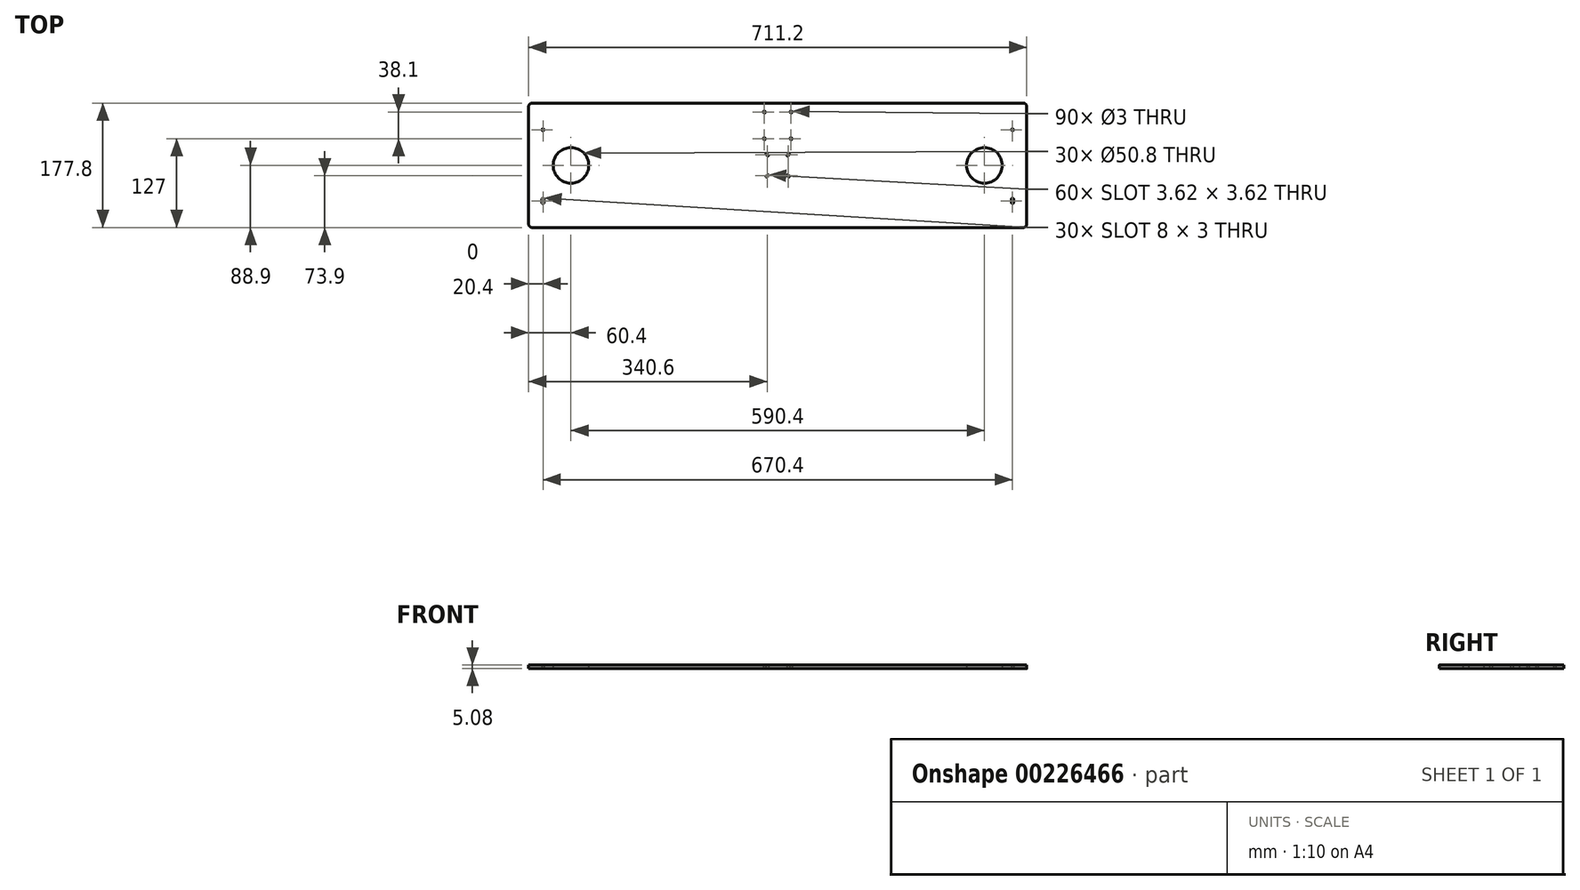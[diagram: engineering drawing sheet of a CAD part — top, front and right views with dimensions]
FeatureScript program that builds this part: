
annotation { "Feature Type Name" : "Feature", "Feature Type Description" : "" }
export const myFeature = defineFeature(function(context is Context, id is Id, definition is map)
    precondition{}
    {
        {
            var Q0;
            Q0=qCreatedBy(makeId("Top.planeOp"),FACE);
            var sketch = newSketch(context, id + "F0", { "sketchPlane" : qUnion([Q0])});
            skLineSegment(sketch, "E0.bottom", {"start": v(350.6, 88.9) * mm, "end": v(-350.6, 88.9) * mm});
            skLineSegment(sketch, "E0.top", {"start": v(350.6, -88.9) * mm, "end": v(-350.6, -88.9) * mm});
            skLineSegment(sketch, "E0.left", {"start": v(355.6, 83.9) * mm, "end": v(355.6, -83.9) * mm});
            skLineSegment(sketch, "E0.right", {"start": v(-355.6, 83.9) * mm, "end": v(-355.6, -83.9) * mm});
            skPoint(sketch, "E0.middle", {"position": v(0, 0) * mm});
            skCircle(sketch, "E1", {"center": v(-335.2, 50.8) * mm, "radius": 1.5 * mm});
            skArc(sketch, "E2", {"start": v(-336.7, -53.3) * mm, "mid": v(-335.2, -54.8) * mm, "end": v(-333.7, -53.3) * mm});
            skArc(sketch, "E3", {"start": v(-333.7, -48.3) * mm, "mid": v(-335.2, -46.8) * mm, "end": v(-336.7, -48.3) * mm});
            skLineSegment(sketch, "E4", {"start": v(-333.7, -48.3) * mm, "end": v(-333.7, -53.3) * mm});
            skLineSegment(sketch, "E5", {"start": v(-336.7, -48.3) * mm, "end": v(-336.7, -53.3) * mm});
            skPoint(sketch, "E6", {"position": v(-333.7, -50.8) * mm});
            skLineSegment(sketch, "E7", {"start": v(-335.2, 50.8) * mm, "end": v(-335.2, -50.8) * mm, "construction": true});
            skPoint(sketch, "E8", {"position": v(-335.2, 0) * mm});
            skLineSegment(sketch, "E9", {"start": v(0, 88.9) * mm, "end": v(0, -88.9) * mm, "construction": true});
            skLineSegment(sketch, "E10.MirrorCS", {"start": v(333.7, -48.3) * mm, "end": v(333.7, -53.3) * mm});
            skLineSegment(sketch, "E11.MirrorCS", {"start": v(336.7, -48.3) * mm, "end": v(336.7, -53.3) * mm});
            skArc(sketch, "E12.MirrorCS", {"start": v(336.7, -53.3) * mm, "mid": v(335.2, -54.8) * mm, "end": v(333.7, -53.3) * mm});
            skCircle(sketch, "E13.MirrorC", {"center": v(335.2, 50.8) * mm, "radius": 1.5 * mm});
            skArc(sketch, "E14.MirrorCS", {"start": v(333.7, -48.3) * mm, "mid": v(335.2, -46.8) * mm, "end": v(336.7, -48.3) * mm});
            skPoint(sketch, "E15.MirrorP", {"position": v(333.7, -50.8) * mm});
            skPoint(sketch, "E16.MirrorP", {"position": v(335.2, 0) * mm});
            skLineSegment(sketch, "E17.MirrorCS", {"start": v(335.2, 50.8) * mm, "end": v(335.2, -50.8) * mm, "construction": true});
            skPoint(sketch, "E18.visualSharp", {"position": v(355.6, 88.9) * mm});
            skArc(sketch, "E18.filletArc", {"start": v(355.6, 83.9) * mm, "mid": v(354.14, 87.44) * mm, "end": v(350.6, 88.9) * mm});
            skPoint(sketch, "E19.visualSharp", {"position": v(355.6, -88.9) * mm});
            skArc(sketch, "E19.filletArc", {"start": v(350.6, -88.9) * mm, "mid": v(354.14, -87.44) * mm, "end": v(355.6, -83.9) * mm});
            skPoint(sketch, "E20.visualSharp", {"position": v(-355.6, -88.9) * mm});
            skArc(sketch, "E20.filletArc", {"start": v(-355.6, -83.9) * mm, "mid": v(-354.14, -87.44) * mm, "end": v(-350.6, -88.9) * mm});
            skPoint(sketch, "E21.visualSharp", {"position": v(-355.6, 88.9) * mm});
            skArc(sketch, "E21.filletArc", {"start": v(-350.6, 88.9) * mm, "mid": v(-354.14, 87.44) * mm, "end": v(-355.6, 83.9) * mm});
            skCircle(sketch, "E22", {"center": v(-19.05, 76.2) * mm, "radius": 1.5 * mm});
            skCircle(sketch, "E23", {"center": v(19.05, 76.2) * mm, "radius": 1.5 * mm});
            skCircle(sketch, "E24", {"center": v(19.05, 38.1) * mm, "radius": 1.5 * mm});
            skCircle(sketch, "E25", {"center": v(-19.05, 38.1) * mm, "radius": 1.5 * mm});
            skLineSegment(sketch, "E26.bottom", {"start": v(-19.05, 76.2) * mm, "end": v(19.05, 76.2) * mm, "construction": true});
            skLineSegment(sketch, "E26.top", {"start": v(-19.05, 38.1) * mm, "end": v(19.05, 38.1) * mm, "construction": true});
            skLineSegment(sketch, "E26.left", {"start": v(-19.05, 76.2) * mm, "end": v(-19.05, 38.1) * mm, "construction": true});
            skLineSegment(sketch, "E26.right", {"start": v(19.05, 76.2) * mm, "end": v(19.05, 38.1) * mm, "construction": true});
            skPoint(sketch, "E27", {"position": v(0, 76.2) * mm});
            skLineSegment(sketch, "E28", {"start": v(355.6, 0) * mm, "end": v(-355.6, 0) * mm, "construction": true});
            skLineSegment(sketch, "E29", {"start": v(-355.6, 88.9) * mm, "end": v(355.6, -88.9) * mm, "construction": true});
            skLineSegment(sketch, "E30", {"start": v(355.6, 88.9) * mm, "end": v(-355.6, -88.9) * mm, "construction": true});
            skLineSegment(sketch, "E31.bottom", {"start": v(15, 15) * mm, "end": v(-15, 15) * mm, "construction": true});
            skLineSegment(sketch, "E31.top", {"start": v(15, -15) * mm, "end": v(-15, -15) * mm, "construction": true});
            skLineSegment(sketch, "E31.left", {"start": v(15, 15) * mm, "end": v(15, -15) * mm, "construction": true});
            skLineSegment(sketch, "E31.right", {"start": v(-15, 15) * mm, "end": v(-15, -15) * mm, "construction": true});
            skArc(sketch, "E32", {"start": v(-16.6, -15.53) * mm, "mid": v(-16.6, -16.6) * mm, "end": v(-15.53, -16.6) * mm});
            skLineSegment(sketch, "E33", {"start": v(-15.53, -16.6) * mm, "end": v(-16.6, -15.53) * mm, "construction": true});
            skLineSegment(sketch, "E34", {"start": v(-15.53, -16.6) * mm, "end": v(-13.4, -14.47) * mm});
            skLineSegment(sketch, "E35", {"start": v(-13.4, -14.47) * mm, "end": v(-14.47, -13.4) * mm});
            skLineSegment(sketch, "E36", {"start": v(-14.47, -13.4) * mm, "end": v(-16.6, -15.53) * mm});
            skArc(sketch, "E37", {"start": v(-13.4, -14.47) * mm, "mid": v(-13.4, -13.4) * mm, "end": v(-14.47, -13.4) * mm});
            skPoint(sketch, "E38", {"position": v(-14.47, -15.53) * mm});
            skLineSegment(sketch, "E39", {"start": v(-14.47, -15.53) * mm, "end": v(-15.53, -14.47) * mm, "construction": true});
            skPoint(sketch, "E40", {"position": v(-15, -15) * mm});
            skArc(sketch, "E41", {"start": v(15.53, -16.6) * mm, "mid": v(16.6, -16.6) * mm, "end": v(16.6, -15.53) * mm});
            skLineSegment(sketch, "E42", {"start": v(16.6, -15.53) * mm, "end": v(15.53, -16.6) * mm, "construction": true});
            skLineSegment(sketch, "E43", {"start": v(16.6, -15.53) * mm, "end": v(14.47, -13.4) * mm});
            skLineSegment(sketch, "E44", {"start": v(14.47, -13.4) * mm, "end": v(13.4, -14.47) * mm});
            skLineSegment(sketch, "E45", {"start": v(13.4, -14.47) * mm, "end": v(15.53, -16.6) * mm});
            skArc(sketch, "E46", {"start": v(14.47, -13.4) * mm, "mid": v(13.4, -13.4) * mm, "end": v(13.4, -14.47) * mm});
            skPoint(sketch, "E47", {"position": v(15.53, -14.47) * mm});
            skLineSegment(sketch, "E48", {"start": v(15.53, -14.47) * mm, "end": v(14.47, -15.53) * mm, "construction": true});
            skPoint(sketch, "E49", {"position": v(15, -15) * mm});
            skArc(sketch, "E50", {"start": v(13.4, 14.47) * mm, "mid": v(13.4, 13.4) * mm, "end": v(14.47, 13.4) * mm});
            skLineSegment(sketch, "E51", {"start": v(14.47, 13.4) * mm, "end": v(13.4, 14.47) * mm, "construction": true});
            skLineSegment(sketch, "E52", {"start": v(14.47, 13.4) * mm, "end": v(16.6, 15.53) * mm});
            skLineSegment(sketch, "E53", {"start": v(16.6, 15.53) * mm, "end": v(15.53, 16.6) * mm});
            skLineSegment(sketch, "E54", {"start": v(15.53, 16.6) * mm, "end": v(13.4, 14.47) * mm});
            skArc(sketch, "E55", {"start": v(16.6, 15.53) * mm, "mid": v(16.6, 16.6) * mm, "end": v(15.53, 16.6) * mm});
            skPoint(sketch, "E56", {"position": v(15.53, 14.47) * mm});
            skLineSegment(sketch, "E57", {"start": v(15.53, 14.47) * mm, "end": v(14.47, 15.53) * mm, "construction": true});
            skPoint(sketch, "E58", {"position": v(15, 15) * mm});
            skArc(sketch, "E59", {"start": v(-14.47, 13.4) * mm, "mid": v(-13.4, 13.4) * mm, "end": v(-13.4, 14.47) * mm});
            skLineSegment(sketch, "E60", {"start": v(-13.4, 14.47) * mm, "end": v(-14.47, 13.4) * mm, "construction": true});
            skLineSegment(sketch, "E61", {"start": v(-13.4, 14.47) * mm, "end": v(-15.53, 16.6) * mm});
            skLineSegment(sketch, "E62", {"start": v(-15.53, 16.6) * mm, "end": v(-16.6, 15.53) * mm});
            skLineSegment(sketch, "E63", {"start": v(-16.6, 15.53) * mm, "end": v(-14.47, 13.4) * mm});
            skArc(sketch, "E64", {"start": v(-15.53, 16.6) * mm, "mid": v(-16.6, 16.6) * mm, "end": v(-16.6, 15.53) * mm});
            skPoint(sketch, "E65", {"position": v(-14.47, 15.53) * mm});
            skLineSegment(sketch, "E66", {"start": v(-14.47, 15.53) * mm, "end": v(-15.53, 14.47) * mm, "construction": true});
            skPoint(sketch, "E67", {"position": v(-15, 15) * mm});
            skCircle(sketch, "E68", {"center": v(295.2, 0) * mm, "radius": 25.4 * mm});
            skCircle(sketch, "E69", {"center": v(-295.2, 0) * mm, "radius": 25.4 * mm});
            skSolve(sketch);
        }
        {
            var Q0;
            Q0=makeQuery(id+"F0.imprint","IMPRINT",FACE,{"disambiguationData":[TD([[makeQuery(id+"F0.imprint","IMPRINT",EDGE,{"derivedFrom":sQuery(id+"F0.wireOp",EDGE,"E0.bottom")}),1.0]])]});
            extrude(context, id + "F1", {"entities" : qUnion([Q0]), "depth" : 5.08 * mm});
        }
    });
